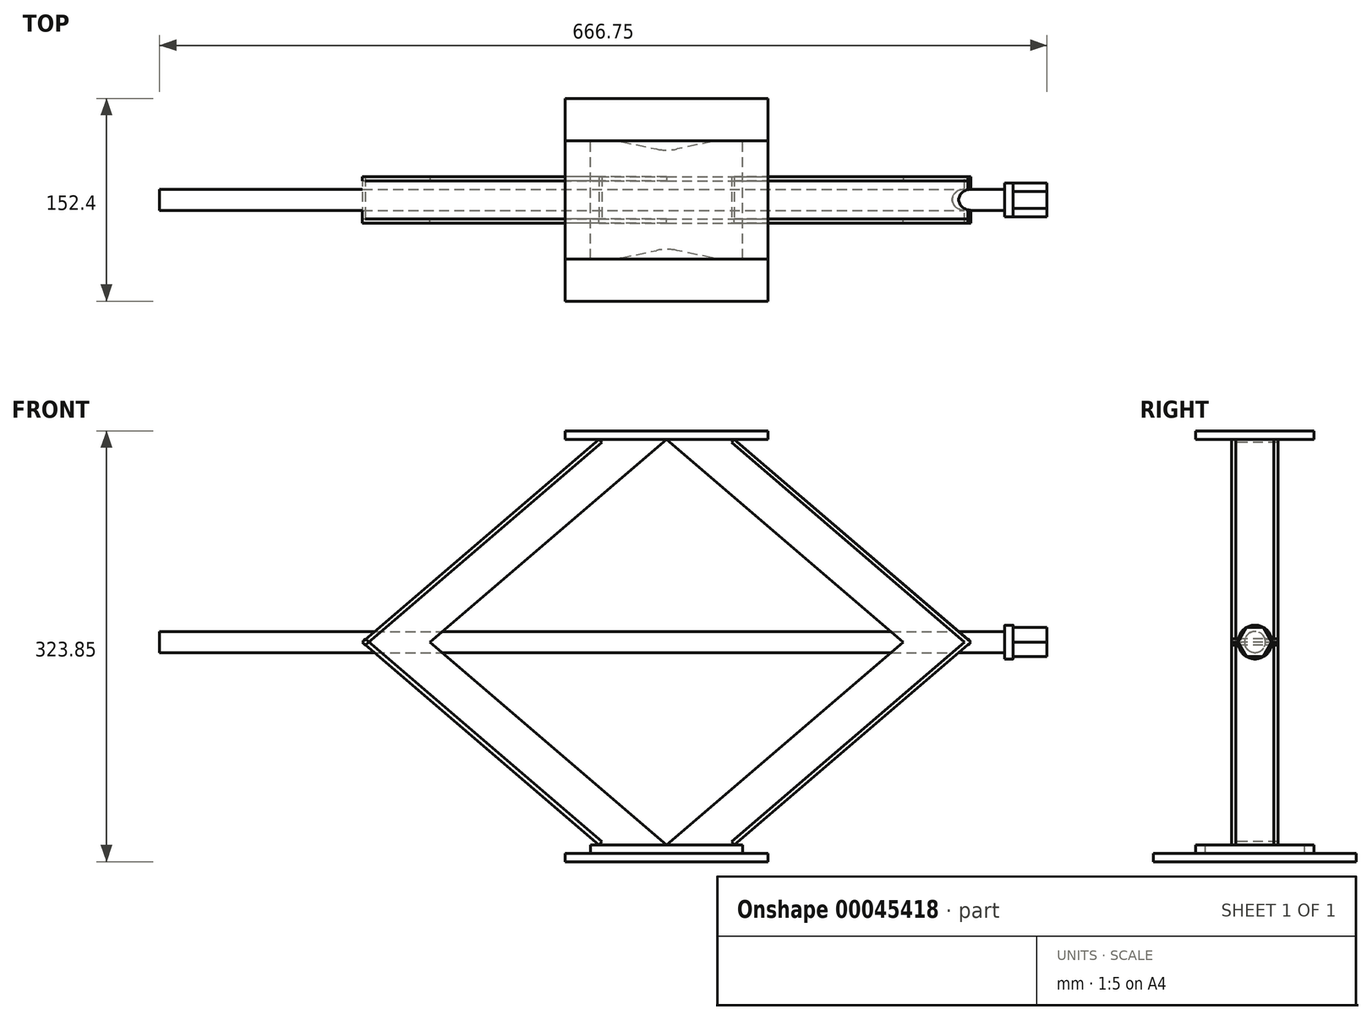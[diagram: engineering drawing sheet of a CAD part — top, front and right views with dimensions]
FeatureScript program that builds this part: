
annotation { "Feature Type Name" : "Feature", "Feature Type Description" : "" }
export const myFeature = defineFeature(function(context is Context, id is Id, definition is map)
    precondition{}
    {
        {
            var Q0;
            Q0=qCreatedBy(makeId("Front.planeOp"),FACE);
            cPlane(context, id + "F0", {"entities" : qUnion([Q0]), "cplaneType" : CPlaneType.OFFSET, "offset" : 14.29 * mm, "width" : 152.4 * mm, "height" : 152.4 * mm});
        }
        {
            var Q0;
            Q0=qCreatedBy(id+"F0.planeOp",FACE);
            var sketch = newSketch(context, id + "F1", { "sketchPlane" : qUnion([Q0])});
            skLineSegment(sketch, "E0", {"start": v(0, 152.4) * mm, "end": v(0, -152.4) * mm, "construction": true});
            skLineSegment(sketch, "E1", {"start": v(0, 152.4) * mm, "end": v(-177.8, 0) * mm});
            skLineSegment(sketch, "E2", {"start": v(-177.8, 0) * mm, "end": v(0, -152.4) * mm});
            skLineSegment(sketch, "E3", {"start": v(-177.8, 0) * mm, "end": v(177.8, 0) * mm, "construction": true});
            skLineSegment(sketch, "E4", {"start": v(0, 152.4) * mm, "end": v(177.8, 0) * mm});
            skLineSegment(sketch, "E5", {"start": v(0, -152.4) * mm, "end": v(177.8, 0) * mm});
            skLineSegment(sketch, "E6", {"start": v(-50.8, 152.4) * mm, "end": v(50.8, 152.4) * mm});
            skLineSegment(sketch, "E7", {"start": v(-50.8, 152.4) * mm, "end": v(-228.6, 0) * mm});
            skLineSegment(sketch, "E8", {"start": v(-228.6, 0) * mm, "end": v(-50.8, -152.4) * mm});
            skLineSegment(sketch, "E9", {"start": v(-228.6, 0) * mm, "end": v(-177.8, 0) * mm, "construction": true});
            skLineSegment(sketch, "E10.MirrorCS", {"start": v(50.8, 152.4) * mm, "end": v(228.6, 0) * mm});
            skLineSegment(sketch, "E11.MirrorCS", {"start": v(228.6, 0) * mm, "end": v(50.8, -152.4) * mm});
            skLineSegment(sketch, "E12", {"start": v(-50.8, -152.4) * mm, "end": v(50.8, -152.4) * mm});
            skLineSegment(sketch, "E13", {"start": v(177.8, 0) * mm, "end": v(228.6, 0) * mm, "construction": true});
            skSolve(sketch);
        }
        {
            var Q0;
            {var subQ3=sQuery(id+"F1.wireOp",EDGE,"E1");Q0=makeQuery(id+"F1.imprint","IMPRINT",FACE,{"disambiguationData":[TD([[makeQuery(id+"F1.imprint","IMPRINT",EDGE,{"derivedFrom":subQ3}),-1.0]])]});}
            var Q1;
            {var subQ3=sQuery(id+"F1.wireOp",EDGE,"E4");Q1=makeQuery(id+"F1.imprint","IMPRINT",FACE,{"disambiguationData":[TD([[makeQuery(id+"F1.imprint","IMPRINT",EDGE,{"derivedFrom":subQ3}),1.0]])]});}
            extrude(context, id + "F2", {"entities" : qUnion([Q0, Q1]), "depth" : 3.17 * mm});
        }
        {
            var Q0;
            Q0=makeQuery(id+"F2.opExtrude","SWEPT_BODY",BODY,{"disambiguationData":[OSD([sQuery(id+"F1.wireOp",EDGE,"E1"),sQuery(id+"F1.wireOp",EDGE,"E2"),sQuery(id+"F1.wireOp",EDGE,"E6"),sQuery(id+"F1.wireOp",EDGE,"E7"),sQuery(id+"F1.wireOp",EDGE,"E8"),sQuery(id+"F1.wireOp",EDGE,"E12")])]});
            var Q1;
            Q1=makeQuery(id+"F2.opExtrude","SWEPT_BODY",BODY,{"disambiguationData":[OSD([sQuery(id+"F1.wireOp",EDGE,"E4"),sQuery(id+"F1.wireOp",EDGE,"E5"),sQuery(id+"F1.wireOp",EDGE,"E6"),sQuery(id+"F1.wireOp",EDGE,"E10.MirrorCS"),sQuery(id+"F1.wireOp",EDGE,"E11.MirrorCS"),sQuery(id+"F1.wireOp",EDGE,"E12")])]});
            var Q2;
            Q2=qCreatedBy(makeId("Front.planeOp"),FACE);
            mirror(context, id + "F3", {"entities" : qUnion([Q0, Q1]), "mirrorPlane" : qUnion([Q2])});
        }
        {
            var Q0;
            Q0=makeQuery(id+"F3.opPattern","COPY",FACE,{"derivedFrom":makeQuery(id+"F2.opExtrude","SWEPT_FACE",FACE,{"disambiguationData":[OSD([sQuery(id+"F1.wireOp",EDGE,"E7")])]}),"instanceName":"1"});
            var sketch = newSketch(context, id + "F4", { "sketchPlane" : qUnion([Q0])});
            skLineSegment(sketch, "E14.bottom", {"start": v(60.61, 17.46) * mm, "end": v(-173.57, 17.46) * mm});
            skLineSegment(sketch, "E14.top", {"start": v(60.61, -17.46) * mm, "end": v(-173.57, -17.46) * mm});
            skLineSegment(sketch, "E14.left", {"start": v(60.61, 17.46) * mm, "end": v(60.61, -17.46) * mm});
            skLineSegment(sketch, "E14.right", {"start": v(-173.57, 17.46) * mm, "end": v(-173.57, -17.46) * mm});
            skSolve(sketch);
        }
        {
            var Q0;
            Q0 = qSketchRegion(id + "F4", true);
            extrude(context, id + "F5", {"entities" : qUnion([Q0]), "oppositeDirection" : true, "depth" : 3.17 * mm});
        }
        {
            var Q0;
            Q0=makeQuery(id+"F5.opExtrude","SWEPT_BODY",BODY,{"disambiguationData":[OSD([sQuery(id+"F4.wireOp",EDGE,"E14.bottom"),sQuery(id+"F4.wireOp",EDGE,"E14.top"),sQuery(id+"F4.wireOp",EDGE,"E14.left"),sQuery(id+"F4.wireOp",EDGE,"E14.right")])]});
            var Q1;
            Q1=qCreatedBy(makeId("Top.planeOp"),FACE);
            mirror(context, id + "F6", {"entities" : qUnion([Q0]), "mirrorPlane" : qUnion([Q1])});
        }
        {
            var Q0;
            Q0=makeQuery(id+"F5.opExtrude","SWEPT_BODY",BODY,{"disambiguationData":[OSD([sQuery(id+"F4.wireOp",EDGE,"E14.bottom"),sQuery(id+"F4.wireOp",EDGE,"E14.top"),sQuery(id+"F4.wireOp",EDGE,"E14.left"),sQuery(id+"F4.wireOp",EDGE,"E14.right")])]});
            var Q1;
            Q1=makeQuery(id+"F6.opPattern","COPY",BODY,{"derivedFrom":makeQuery(id+"F5.opExtrude","SWEPT_BODY",BODY,{"disambiguationData":[OSD([sQuery(id+"F4.wireOp",EDGE,"E14.bottom"),sQuery(id+"F4.wireOp",EDGE,"E14.top"),sQuery(id+"F4.wireOp",EDGE,"E14.left"),sQuery(id+"F4.wireOp",EDGE,"E14.right")])]}),"instanceName":"1"});
            var Q2;
            Q2=qCreatedBy(makeId("Right.planeOp"),FACE);
            mirror(context, id + "F7", {"entities" : qUnion([Q0, Q1]), "mirrorPlane" : qUnion([Q2])});
        }
        {
            var Q0;
            {var subQ0=sQuery(id+"F1.wireOp",EDGE,"E6");Q0=makeQuery(id+"F2.opExtrude","SWEPT_FACE",FACE,{"disambiguationData":[OSD([subQ0]),TDD([makeQuery(id+"F1.imprint","IMPRINT",EDGE,{"disambiguationData":[TD([[makeQuery(id+"F1.imprint","INTERSECT",VERTEX,{"derivedFrom":[subQ0,sQuery(id+"F1.wireOp",EDGE,"E10.MirrorCS")]}),1.0]])],"derivedFrom":subQ0})])]});}
            var sketch = newSketch(context, id + "F8", { "sketchPlane" : qUnion([Q0])});
            skLineSegment(sketch, "E15.rect.bottom", {"start": v(76.2, -44.45) * mm, "end": v(-76.2, -44.45) * mm});
            skLineSegment(sketch, "E15.rect.top", {"start": v(76.2, 44.45) * mm, "end": v(-76.2, 44.45) * mm});
            skLineSegment(sketch, "E15.rect.left", {"start": v(76.2, -44.45) * mm, "end": v(76.2, 44.45) * mm});
            skLineSegment(sketch, "E15.rect.right", {"start": v(-76.2, -44.45) * mm, "end": v(-76.2, 44.45) * mm});
            skPoint(sketch, "E15.rect.middle", {"position": v(0, 0) * mm});
            skSolve(sketch);
        }
        {
            var Q0;
            Q0 = qSketchRegion(id + "F8", true);
            extrude(context, id + "F9", {"entities" : qUnion([Q0]), "depth" : 6.35 * mm});
        }
        {
            var Q0;
            {var subQ0=sQuery(id+"F1.wireOp",EDGE,"E12");Q0=makeQuery(id+"F2.opExtrude","SWEPT_FACE",FACE,{"disambiguationData":[OSD([subQ0]),TDD([makeQuery(id+"F1.imprint","IMPRINT",EDGE,{"disambiguationData":[TD([[makeQuery(id+"F1.imprint","INTERSECT",VERTEX,{"derivedFrom":[sQuery(id+"F1.wireOp",EDGE,"E11.MirrorCS"),subQ0]}),1.0]])],"derivedFrom":subQ0})])]});}
            var sketch = newSketch(context, id + "F10", { "sketchPlane" : qUnion([Q0])});
            skLineSegment(sketch, "E16", {"start": v(0, 36.51) * mm, "end": v(0, -36.51) * mm, "construction": true});
            skLineSegment(sketch, "E17", {"start": v(-57.15, 44.45) * mm, "end": v(-57.15, -44.45) * mm});
            skLineSegment(sketch, "E18", {"start": v(-57.15, 0) * mm, "end": v(0, 0) * mm, "construction": true});
            skLineSegment(sketch, "E19", {"start": v(-57.15, 44.45) * mm, "end": v(-42.03, 44.45) * mm});
            skLineSegment(sketch, "E20", {"start": v(-34.26, 43.65) * mm, "end": v(-7.77, 38.13) * mm});
            skLineSegment(sketch, "E21.MirrorCS", {"start": v(-34.26, -43.65) * mm, "end": v(-7.77, -38.13) * mm});
            skLineSegment(sketch, "E22.MirrorCS", {"start": v(-57.15, -44.45) * mm, "end": v(-42.03, -44.45) * mm});
            skLineSegment(sketch, "E23.MirrorCS", {"start": v(34.26, 43.65) * mm, "end": v(7.77, 38.13) * mm});
            skLineSegment(sketch, "E24.MirrorCS", {"start": v(57.15, 44.45) * mm, "end": v(42.03, 44.45) * mm});
            skLineSegment(sketch, "E25.MirrorCS", {"start": v(57.15, 44.45) * mm, "end": v(57.15, -44.45) * mm});
            skLineSegment(sketch, "E26.MirrorCS", {"start": v(57.15, -44.45) * mm, "end": v(42.03, -44.45) * mm});
            skLineSegment(sketch, "E27.MirrorCS", {"start": v(34.26, -43.65) * mm, "end": v(7.77, -38.13) * mm});
            skPoint(sketch, "E28.visualSharp", {"position": v(-38.1, 44.45) * mm});
            skArc(sketch, "E28.filletArc", {"start": v(-34.26, 43.65) * mm, "mid": v(-38.12, 44.25) * mm, "end": v(-42.03, 44.45) * mm});
            skPoint(sketch, "E29.visualSharp", {"position": v(0, 36.51) * mm});
            skArc(sketch, "E29.filletArc", {"start": v(-7.77, 38.13) * mm, "mid": v(0, 37.33) * mm, "end": v(7.77, 38.13) * mm});
            skPoint(sketch, "E30.visualSharp", {"position": v(38.1, 44.45) * mm});
            skArc(sketch, "E30.filletArc", {"start": v(42.03, 44.45) * mm, "mid": v(38.12, 44.25) * mm, "end": v(34.26, 43.65) * mm});
            skPoint(sketch, "E31.visualSharp", {"position": v(0, -36.51) * mm});
            skArc(sketch, "E31.filletArc", {"start": v(7.77, -38.13) * mm, "mid": v(0, -37.33) * mm, "end": v(-7.77, -38.13) * mm});
            skPoint(sketch, "E32.visualSharp", {"position": v(-38.1, -44.45) * mm});
            skArc(sketch, "E32.filletArc", {"start": v(-42.03, -44.45) * mm, "mid": v(-38.12, -44.25) * mm, "end": v(-34.26, -43.65) * mm});
            skPoint(sketch, "E33.visualSharp", {"position": v(38.1, -44.45) * mm});
            skArc(sketch, "E33.filletArc", {"start": v(34.26, -43.65) * mm, "mid": v(38.12, -44.25) * mm, "end": v(42.03, -44.45) * mm});
            skSolve(sketch);
        }
        {
            var Q0;
            Q0 = qSketchRegion(id + "F10", true);
            extrude(context, id + "F11", {"entities" : qUnion([Q0]), "depth" : 6.35 * mm});
        }
        {
            var Q0;
            Q0=qCreatedBy(makeId("Right.planeOp"),FACE);
            cPlane(context, id + "F12", {"entities" : qUnion([Q0]), "cplaneType" : CPlaneType.OFFSET, "offset" : 228.6 * mm, "width" : 152.4 * mm, "height" : 152.4 * mm});
        }
        {
            var Q0;
            Q0=qCreatedBy(id+"F12.planeOp",FACE);
            var sketch = newSketch(context, id + "F13", { "sketchPlane" : qUnion([Q0])});
            skCircle(sketch, "E34", {"center": v(0, 0) * mm, "radius": 7.94 * mm});
            skSolve(sketch);
        }
        {
            var Q0;
            Q0 = qSketchRegion(id + "F13", true);
            extrude(context, id + "F14", {"entities" : qUnion([Q0]), "oppositeDirection" : true, "depth" : 609.6 * mm});
        }
        {
            var Q0;
            Q0=makeQuery(id+"F14.opExtrude","CAP_FACE",FACE,{"disambiguationData":[OSD([sQuery(id+"F13.wireOp",EDGE,"E34")])],"isStart":true});
            var sketch = newSketch(context, id + "F15", { "sketchPlane" : qUnion([Q0])});
            skCircle(sketch, "E35", {"center": v(0, 0) * mm, "radius": 7.94 * mm});
            skSolve(sketch);
        }
        {
            var Q0;
            Q0 = qSketchRegion(id + "F15", true);
            extrude(context, id + "F16", {"entities" : qUnion([Q0]), "operationType" : NewBodyOperationType.ADD, "depth" : 25.4 * mm});
        }
        {
            var Q0;
            Q0=makeQuery(id+"F16.opExtrude","CAP_FACE",FACE,{"disambiguationData":[OSD([sQuery(id+"F15.wireOp",EDGE,"E35")])],"isStart":false});
            var sketch = newSketch(context, id + "F17", { "sketchPlane" : qUnion([Q0])});
            skCircle(sketch, "E36", {"center": v(0, 0) * mm, "radius": 12.7 * mm});
            skSolve(sketch);
        }
        {
            var Q0;
            Q0 = qSketchRegion(id + "F17", true);
            extrude(context, id + "F18", {"entities" : qUnion([Q0]), "operationType" : NewBodyOperationType.ADD, "depth" : 6.35 * mm});
        }
        {
            var Q0;
            Q0=makeQuery(id+"F18.opExtrude","CAP_FACE",FACE,{"disambiguationData":[OSD([sQuery(id+"F17.wireOp",EDGE,"E36")])],"isStart":false});
            var sketch = newSketch(context, id + "F19", { "sketchPlane" : qUnion([Q0])});
            skCircle(sketch, "E37.cCircle", {"center": v(0, 0) * mm, "radius": 12.7 * mm, "construction": true});
            skLineSegment(sketch, "E37.0", {"start": v(6.35, 11) * mm, "end": v(12.7, 0) * mm});
            skLineSegment(sketch, "E37.1", {"start": v(12.7, 0) * mm, "end": v(6.35, -11) * mm});
            skLineSegment(sketch, "E37.2", {"start": v(6.35, -11) * mm, "end": v(-6.35, -11) * mm});
            skLineSegment(sketch, "E37.3", {"start": v(-6.35, -11) * mm, "end": v(-12.7, 0) * mm});
            skLineSegment(sketch, "E37.4", {"start": v(-12.7, 0) * mm, "end": v(-6.35, 11) * mm});
            skLineSegment(sketch, "E37.5", {"start": v(-6.35, 11) * mm, "end": v(6.35, 11) * mm});
            skSolve(sketch);
        }
        {
            var Q0;
            Q0 = qSketchRegion(id + "F19", true);
            extrude(context, id + "F20", {"entities" : qUnion([Q0]), "operationType" : NewBodyOperationType.ADD, "depth" : 25.4 * mm});
        }
        {
            var Q0;
            Q0=makeQuery(id+"F11.opExtrude","CAP_FACE",FACE,{"disambiguationData":[OSD([sQuery(id+"F10.wireOp",EDGE,"E17"),sQuery(id+"F10.wireOp",EDGE,"E19"),sQuery(id+"F10.wireOp",EDGE,"E20"),sQuery(id+"F10.wireOp",EDGE,"E21.MirrorCS"),sQuery(id+"F10.wireOp",EDGE,"E22.MirrorCS"),sQuery(id+"F10.wireOp",EDGE,"E23.MirrorCS"),sQuery(id+"F10.wireOp",EDGE,"E24.MirrorCS"),sQuery(id+"F10.wireOp",EDGE,"E25.MirrorCS"),sQuery(id+"F10.wireOp",EDGE,"E26.MirrorCS"),sQuery(id+"F10.wireOp",EDGE,"E27.MirrorCS"),sQuery(id+"F10.wireOp",EDGE,"E28.filletArc"),sQuery(id+"F10.wireOp",EDGE,"E29.filletArc"),sQuery(id+"F10.wireOp",EDGE,"E30.filletArc"),sQuery(id+"F10.wireOp",EDGE,"E31.filletArc"),sQuery(id+"F10.wireOp",EDGE,"E32.filletArc"),sQuery(id+"F10.wireOp",EDGE,"E33.filletArc")])],"isStart":false});
            var sketch = newSketch(context, id + "F21", { "sketchPlane" : qUnion([Q0])});
            skLineSegment(sketch, "E38.rect.bottom", {"start": v(76.2, 76.2) * mm, "end": v(-76.2, 76.2) * mm});
            skLineSegment(sketch, "E38.rect.top", {"start": v(76.2, -76.2) * mm, "end": v(-76.2, -76.2) * mm});
            skLineSegment(sketch, "E38.rect.left", {"start": v(76.2, 76.2) * mm, "end": v(76.2, -76.2) * mm});
            skLineSegment(sketch, "E38.rect.right", {"start": v(-76.2, 76.2) * mm, "end": v(-76.2, -76.2) * mm});
            skPoint(sketch, "E38.rect.middle", {"position": v(0, 0) * mm});
            skSolve(sketch);
        }
        {
            var Q0;
            Q0 = qSketchRegion(id + "F21", true);
            extrude(context, id + "F22", {"entities" : qUnion([Q0]), "operationType" : NewBodyOperationType.ADD, "depth" : 6.35 * mm});
        }
    });
